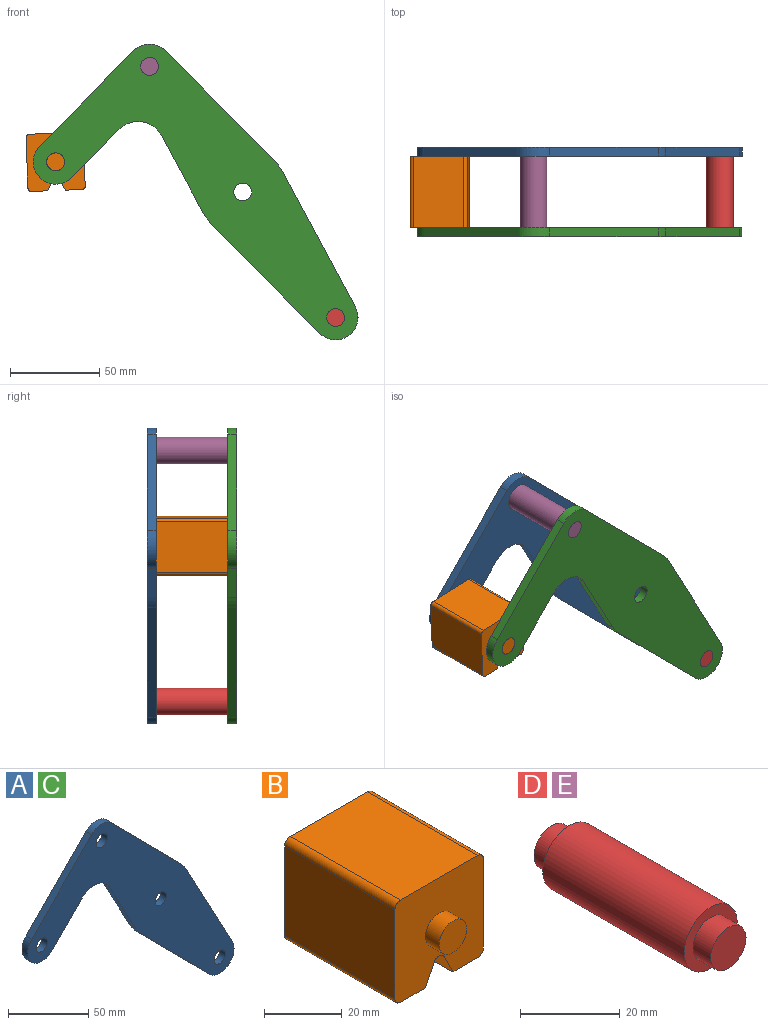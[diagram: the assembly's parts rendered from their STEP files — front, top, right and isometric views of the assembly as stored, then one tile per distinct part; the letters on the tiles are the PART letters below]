
ASSEMBLY  parts=5 mates=3
PART A: 18 faces, bbox 181.7x5x165.8 mm
  f0: plane 43.49x23.35mm, normal (-0.88,0,-0.47), area 246.8mm2, adj f1,f14,f16,f17
  f1: cylinder r=25mm len=5.75mm, axis (0,1,0), area 35.8mm2, adj f0,f2,f16,f17
  f2: plane 61.6x60.87mm, normal (-0.71,0,-0.7), area 433mm2, adj f1,f3,f16,f17
  f3: cylinder r=12.5mm len=21.39mm, axis (0,1,0), area 178.4mm2, adj f2,f4,f16,f17
  f4: plane 76.3x40.96mm, normal (0.88,0,0.47), area 433mm2, adj f3,f5,f16,f17
  f5: cylinder r=25mm len=5.75mm, axis (0,1,0), area 35.8mm2, adj f4,f6,f16,f17
  f6: plane 61.6x60.87mm, normal (0.71,0,0.7), area 433mm2, adj f5,f7,f16,f17
  f7: cylinder r=12.5mm len=17.78mm, axis (0,1,0), area 98.9mm2, adj f6,f8,f16,f17
  f8: plane 53.35x52.71mm, normal (-0.71,0,0.7), area 375mm2, adj f7,f9,f16,f17
  f9: cylinder r=12.5mm len=21.39mm, axis (0,1,0), area 196.3mm2, adj f8,f10,f16,f17
  f10: plane 26.86x26.54mm, normal (0.71,0,-0.7), area 188.8mm2, adj f9,f14,f16,f17
  f11: cylinder r=5mm len=10mm, axis (0,1,0), area 157.1mm2, adj f16,f17
  f12: cylinder r=5mm len=10mm, axis (0,1,0), area 157.1mm2, adj f16,f17
  f13: cylinder r=5mm len=10mm, axis (0,1,0), area 157.1mm2, adj f16,f17
  f14: cylinder r=15mm len=23.89mm, axis (0,1,0), area 140.2mm2, adj f0,f10,f16,f17
  f15: cylinder r=5mm len=10mm, axis (0,1,0), area 157.1mm2, adj f16,f17
  f16: plane 181.66x165.78mm, normal (0,-1,0), area 8710.1mm2, adj f0,f1,f2,f3,f4,f5,f6,f7
  f17: plane 181.66x165.78mm, normal (0,1,0), area 8710.1mm2, adj f0,f1,f2,f3,f4,f5,f6,f7
PART B: 18 faces, bbox 32.1x50x32.1 mm
  f0: plane 40x28.08mm, normal (1,0,0), area 1123.1mm2, adj f4,f10,f13,f14
  f1: plane 40x9.04mm, normal (0,0,-1), area 361.6mm2, adj f2,f4,f10,f14
  f2: plane 40x6.42mm, normal (-0.89,0,-0.45), area 287.2mm2, adj f1,f4,f10,f15
  f3: plane 40x6.42mm, normal (0.89,0,-0.45), area 287.2mm2, adj f4,f5,f10,f15
  f4: plane 32.08x32.08mm, normal (0,-1,0), area 900.6mm2, adj f0,f1,f2,f3,f5,f6,f7,f9
  f5: plane 40x9.04mm, normal (0,0,-1), area 361.6mm2, adj f3,f4,f10,f16
  f6: plane 40x28.08mm, normal (0,0,1), area 1123.1mm2, adj f4,f10,f13,f17
  f7: plane 40x28.08mm, normal (-1,0,0), area 1123.1mm2, adj f4,f10,f16,f17
  f8: plane 10x10mm, normal (0,-1,0), area 78.5mm2, adj f9
  f9: cylinder r=5mm len=10mm, axis (0,1,0), area 157.1mm2, adj f4,f8
  f10: plane 32.08x32.08mm, normal (0,1,0), area 900.6mm2, adj f0,f1,f2,f3,f5,f6,f7,f12
  f11: plane 10x10mm, normal (0,1,0), area 78.5mm2, adj f12
  f12: cylinder r=5mm len=10mm, axis (0,-1,0), area 157.1mm2, adj f10,f11
  f13: cylinder r=2mm len=40mm, axis (0,1,0), area 125.7mm2, adj f0,f4,f6,f10
  f14: cylinder r=2mm len=40mm, axis (0,-1,0), area 125.7mm2, adj f0,f1,f4,f10
  f15: cylinder r=2mm len=40mm, axis (0,1,0), area 177.1mm2, adj f2,f3,f4,f10
  f16: cylinder r=2mm len=40mm, axis (0,1,0), area 125.7mm2, adj f4,f5,f7,f10
  f17: cylinder r=2mm len=40mm, axis (0,-1,0), area 125.7mm2, adj f4,f6,f7,f10
PART C: same geometry as A
PART D: 7 faces, bbox 15x50x15 mm
  f0: cylinder r=7.5mm len=40mm, axis (0,-1,0), area 1885mm2, adj f2,f5
  f1: cylinder r=5mm len=10mm, axis (0,1,0), area 157.1mm2, adj f2,f3
  f2: plane 15x15mm, normal (0,-1,0), area 98.2mm2, adj f0,f1
  f3: plane 10x10mm, normal (0,-1,0), area 78.5mm2, adj f1
  f4: cylinder r=5mm len=10mm, axis (0,-1,0), area 157.1mm2, adj f5,f6
  f5: plane 15x15mm, normal (0,1,0), area 98.2mm2, adj f0,f4
  f6: plane 10x10mm, normal (0,1,0), area 78.5mm2, adj f4
PART E: same geometry as D
PLACE A rot(axis=(0,-1,0),0.1deg) t=(0,25,0)mm
PLACE B rot(axis=(0,-1,0),2.2deg) t=(0.55,-20,3.89)mm
PLACE C rot(axis=(0,-1,0),0.1deg) t=(0,-20,0)mm fixed
PLACE D rot(axis=(0,-1,0),0.1deg) t=(104.18,-20,-140.61)mm
PLACE E rot(axis=(0,-1,0),0.1deg) t=(0,-20,0)mm
MATE revolute B.f9 <-> C.f9  axis (0,-1,0) through (-104.72,-20,16.87)mm
MATE fastened D.f0 <-> C.f3  axis (0,-1,0) through (52.09,-20,-70.31)mm
MATE fastened E.f0 <-> A.f7  axis (0,1,0) through (-52.09,20,70.31)mm
